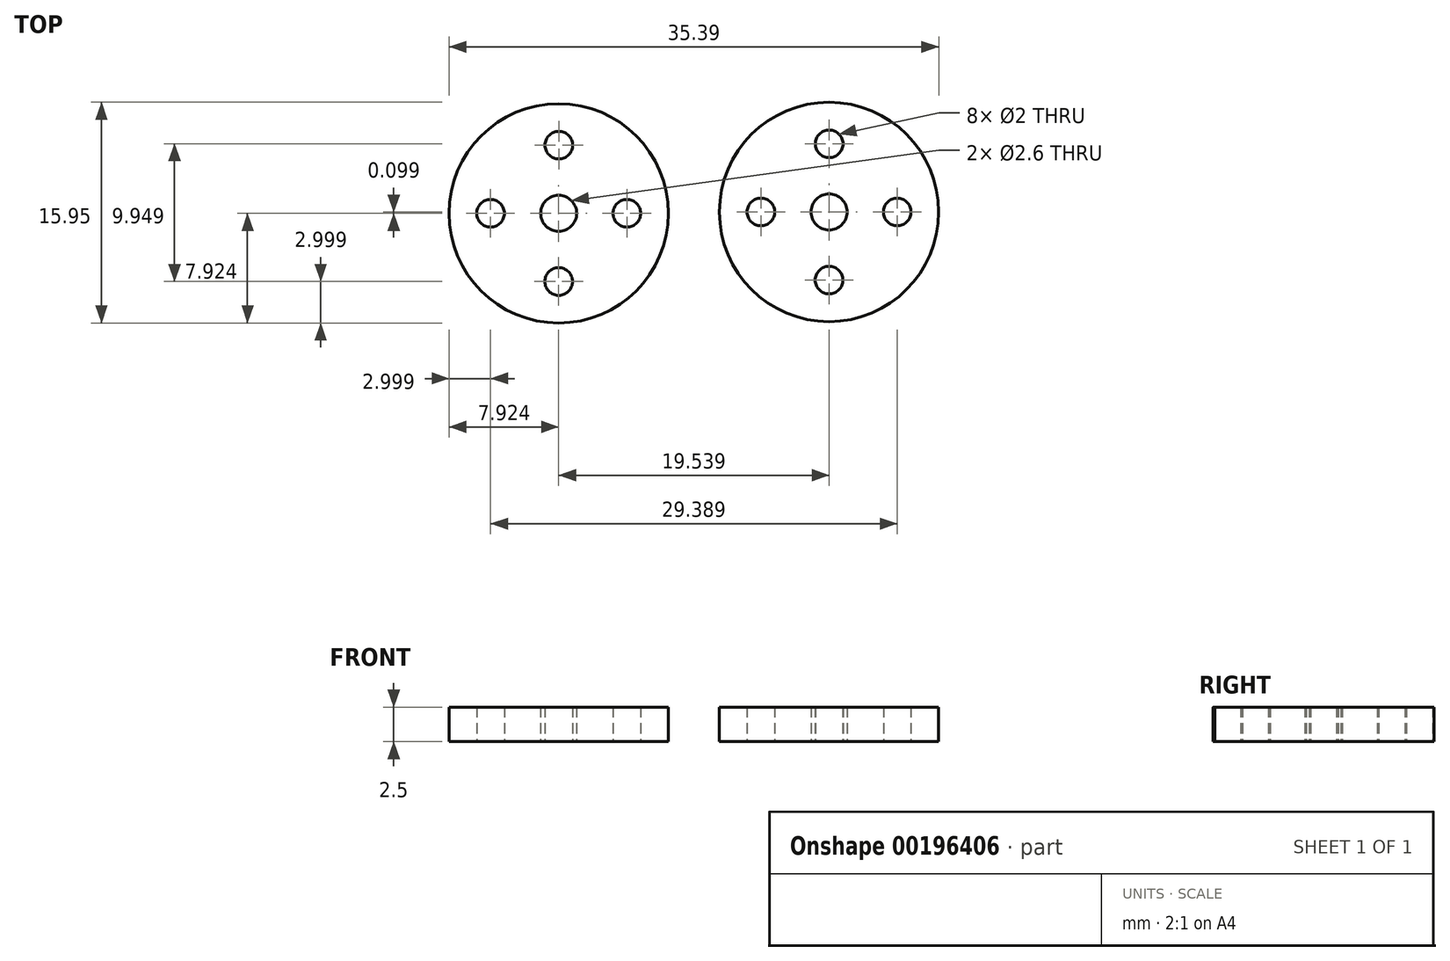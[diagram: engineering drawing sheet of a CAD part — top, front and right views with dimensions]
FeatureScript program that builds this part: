
annotation { "Feature Type Name" : "Feature", "Feature Type Description" : "" }
export const myFeature = defineFeature(function(context is Context, id is Id, definition is map)
    precondition{}
    {
        {
            var Q0;
            Q0=qCreatedBy(makeId("Top.planeOp"),FACE);
            var sketch = newSketch(context, id + "F0", { "sketchPlane" : qUnion([Q0])});
            skCircle(sketch, "E0", {"center": v(-54.77, 19.82) * mm, "radius": 7.92 * mm});
            skCircle(sketch, "E1", {"center": v(-54.77, 19.82) * mm, "radius": 1.3 * mm});
            skCircle(sketch, "E2", {"center": v(-54.76, 24.75) * mm, "radius": 1 * mm});
            skCircle(sketch, "E3", {"center": v(-54.77, 14.9) * mm, "radius": 1 * mm});
            skCircle(sketch, "E4", {"center": v(-49.84, 19.82) * mm, "radius": 1 * mm});
            skCircle(sketch, "E5", {"center": v(-59.7, 19.82) * mm, "radius": 1 * mm});
            skCircle(sketch, "E6", {"center": v(-35.23, 19.92) * mm, "radius": 7.92 * mm});
            skCircle(sketch, "E7", {"center": v(-35.23, 19.92) * mm, "radius": 1.3 * mm});
            skCircle(sketch, "E8", {"center": v(-35.22, 24.85) * mm, "radius": 1 * mm});
            skCircle(sketch, "E9", {"center": v(-35.23, 15) * mm, "radius": 1 * mm});
            skCircle(sketch, "E10", {"center": v(-30.3, 19.92) * mm, "radius": 1 * mm});
            skCircle(sketch, "E11", {"center": v(-40.15, 19.92) * mm, "radius": 1 * mm});
            skSolve(sketch);
        }
        {
            var Q0;
            Q0=makeQuery(id+"F0.imprint","IMPRINT",FACE,{"disambiguationData":[TD([[makeQuery(id+"F0.imprint","IMPRINT",EDGE,{"derivedFrom":sQuery(id+"F0.wireOp",EDGE,"E0")}),1.0]])]});
            var Q1;
            Q1=makeQuery(id+"F0.imprint","IMPRINT",FACE,{"disambiguationData":[TD([[makeQuery(id+"F0.imprint","IMPRINT",EDGE,{"derivedFrom":sQuery(id+"F0.wireOp",EDGE,"E6")}),1.0]])]});
            extrude(context, id + "F1", {"entities" : qUnion([Q0, Q1]), "depth" : 2.5 * mm});
        }
    });
